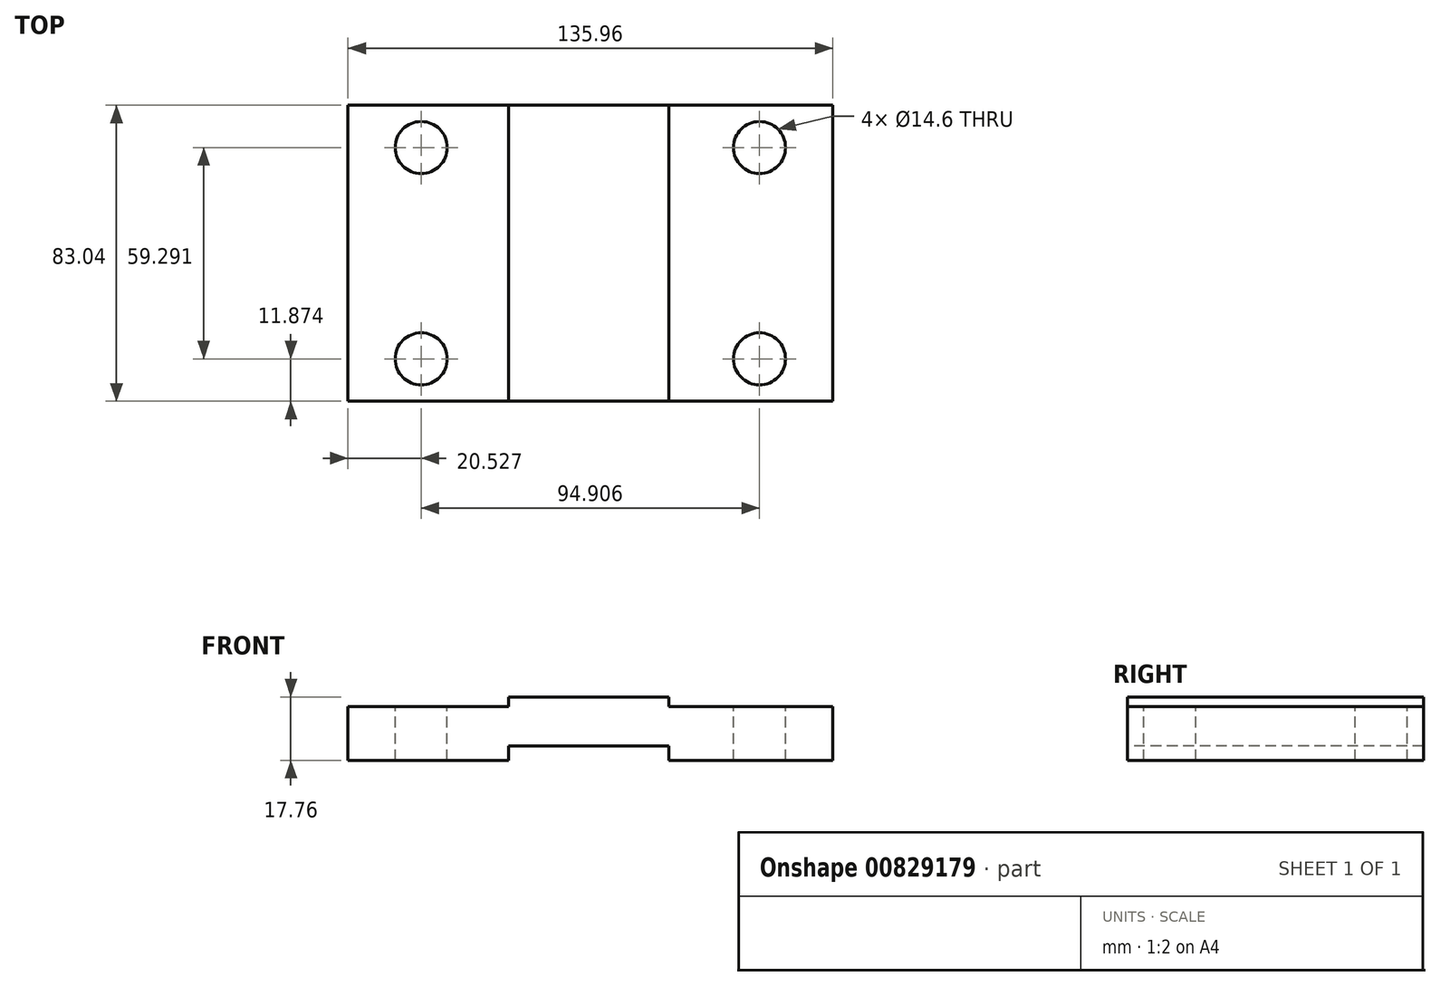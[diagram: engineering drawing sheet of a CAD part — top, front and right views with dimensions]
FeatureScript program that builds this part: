
annotation { "Feature Type Name" : "Feature", "Feature Type Description" : "" }
export const myFeature = defineFeature(function(context is Context, id is Id, definition is map)
    precondition{}
    {
        {
            var Q0;
            Q0=qCreatedBy(makeId("Top.planeOp"),FACE);
            var sketch = newSketch(context, id + "F0", { "sketchPlane" : qUnion([Q0])});
            skLineSegment(sketch, "E0.bottom", {"start": v(-67.98, 41.52) * mm, "end": v(67.98, 41.52) * mm});
            skLineSegment(sketch, "E0.top", {"start": v(-67.98, -41.52) * mm, "end": v(67.98, -41.52) * mm});
            skLineSegment(sketch, "E0.left", {"start": v(-67.98, 41.52) * mm, "end": v(-67.98, -41.52) * mm});
            skLineSegment(sketch, "E0.right", {"start": v(67.98, 41.52) * mm, "end": v(67.98, -41.52) * mm});
            skPoint(sketch, "E0.middle", {"position": v(0, 0) * mm});
            skLineSegment(sketch, "E1", {"start": v(-22.98, 41.52) * mm, "end": v(-22.98, -41.52) * mm});
            skLineSegment(sketch, "E2.1.0.0", {"start": v(22.02, 41.52) * mm, "end": v(22.02, -41.52) * mm});
            skLineSegment(sketch, "E2.direction1", {"start": v(-22.98, -41.52) * mm, "end": v(22.02, -41.52) * mm, "construction": true});
            skSolve(sketch);
        }
        {
            var Q0;
            Q0 = qSketchRegion(id + "F0", true);
            extrude(context, id + "F1", {"entities" : qUnion([Q0]), "oppositeDirection" : true, "depth" : 15 * mm, "offsetDistance" : 25 * mm});
        }
        {
            var Q0;
            {var subQ0=sQuery(id+"F0.wireOp",EDGE,"E1");Q0=makeQuery(id+"F0.imprint","IMPRINT",FACE,{"disambiguationData":[TD([[makeQuery(id+"F0.imprint","IMPRINT",EDGE,{"derivedFrom":subQ0}),1.0]])]});}
            extrude(context, id + "F2", {"entities" : qUnion([Q0]), "operationType" : NewBodyOperationType.ADD, "depth" : 2.76 * mm, "offsetDistance" : 25 * mm});
        }
        {
            var Q0;
            Q0=makeQuery(id+"F1.opExtrude","CAP_FACE",FACE,{"disambiguationData":[OSD([sQuery(id+"F0.wireOp",EDGE,"E0.bottom"),sQuery(id+"F0.wireOp",EDGE,"E0.top"),sQuery(id+"F0.wireOp",EDGE,"E0.left"),sQuery(id+"F0.wireOp",EDGE,"E0.right")])],"isStart":false});
            var sketch = newSketch(context, id + "F3", { "sketchPlane" : qUnion([Q0])});
            skLineSegment(sketch, "E3.0", {"start": v(-22.98, -41.52) * mm, "end": v(-22.98, 41.52) * mm});
            skLineSegment(sketch, "E4.0", {"start": v(22.02, -41.52) * mm, "end": v(22.02, 41.52) * mm});
            skSolve(sketch);
        }
        {
            var Q0;
            Q0 = qSketchRegion(id + "F3", true);
            var Q1;
            {var subQ0=sQuery(id+"F3.wireOp",EDGE,"E3.0");Q1=makeQuery(id+"F3.imprint","IMPRINT",FACE,{"disambiguationData":[TD([[makeQuery(id+"F3.imprint","IMPRINT",EDGE,{"derivedFrom":subQ0}),-1.0]])]});}
            extrude(context, id + "F4", {"entities" : qUnion([Q0, Q1]), "operationType" : NewBodyOperationType.REMOVE, "oppositeDirection" : true, "depth" : 4 * mm, "offsetDistance" : 25 * mm});
        }
        {
            var Q0;
            {var subQ0=sQuery(id+"F0.wireOp",EDGE,"E0.left");Q0=makeQuery(id+"F0.imprint","IMPRINT",FACE,{"disambiguationData":[TD([[makeQuery(id+"F0.imprint","IMPRINT",EDGE,{"derivedFrom":subQ0}),1.0]])]});}
            var sketch = newSketch(context, id + "F5", { "sketchPlane" : qUnion([Q0])});
            skLineSegment(sketch, "E5.0", {"start": v(-67.98, 41.52) * mm, "end": v(-67.98, -41.52) * mm});
            skCircle(sketch, "E6", {"center": v(-47.45, 29.65) * mm, "radius": 7.3 * mm});
            skLineSegment(sketch, "E7", {"start": v(0, 44.98) * mm, "end": v(0, -44.07) * mm});
            skLineSegment(sketch, "E8", {"start": v(-67.98, 0) * mm, "end": v(0, 0) * mm});
            skCircle(sketch, "E9.MirrorC", {"center": v(-47.45, -29.65) * mm, "radius": 7.3 * mm});
            skCircle(sketch, "E10.MirrorC", {"center": v(47.45, 29.65) * mm, "radius": 7.3 * mm});
            skCircle(sketch, "E11.MirrorC", {"center": v(47.45, -29.65) * mm, "radius": 7.3 * mm});
            skSolve(sketch);
        }
        {
            var Q0;
            Q0 = qSketchRegion(id + "F5", true);
            extrude(context, id + "F6", {"entities" : qUnion([Q0]), "operationType" : NewBodyOperationType.REMOVE, "endBound" : BoundingType.THROUGH_ALL, "oppositeDirection" : true, "depth" : 25 * mm, "offsetDistance" : 25 * mm});
        }
    });
